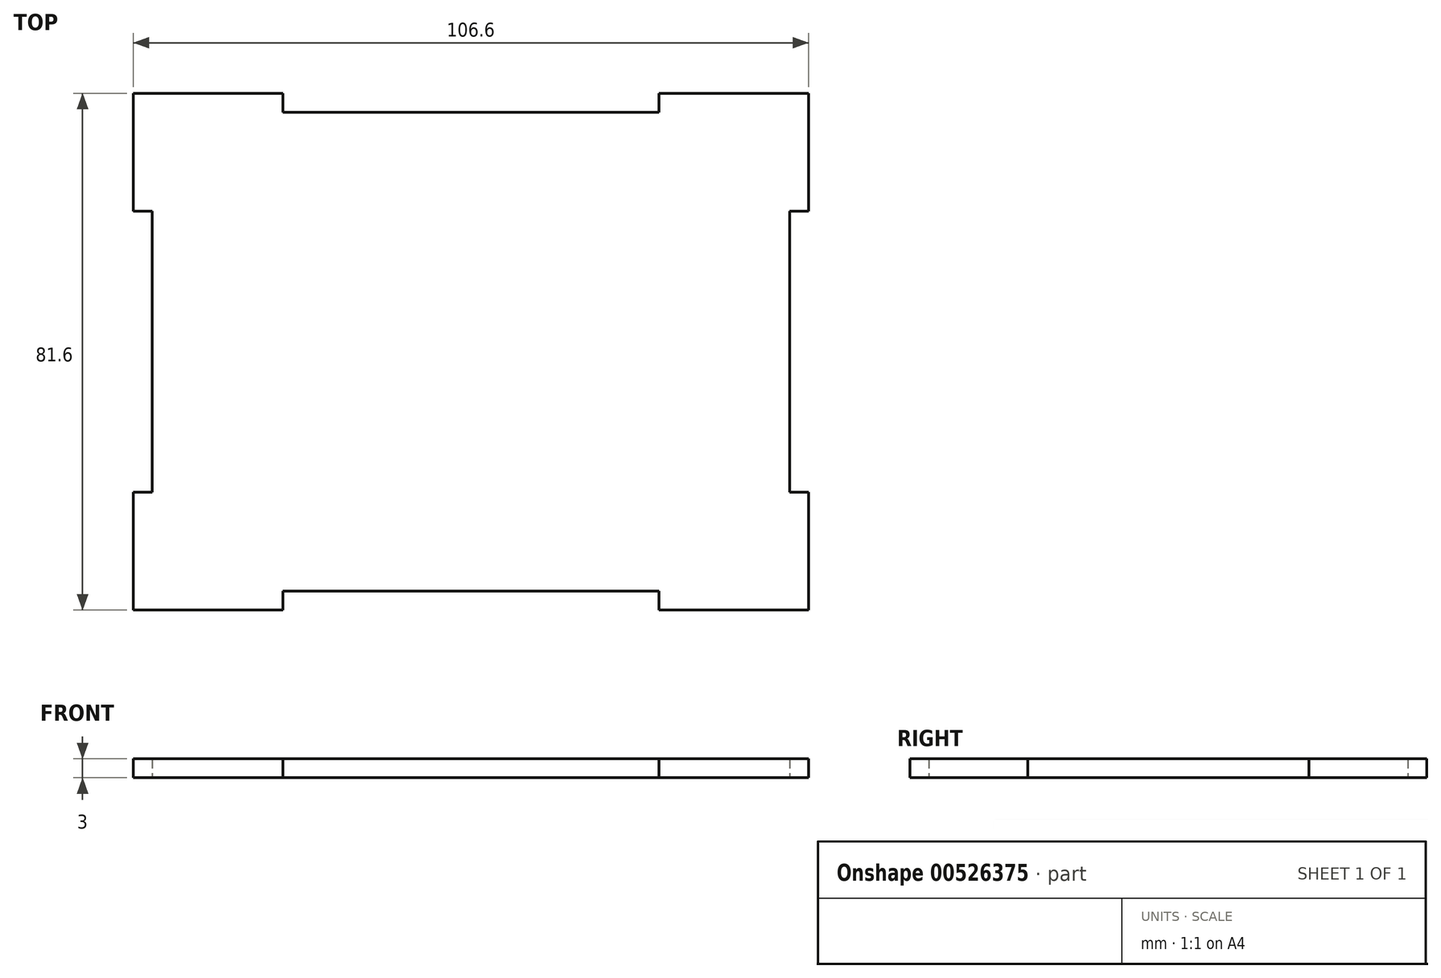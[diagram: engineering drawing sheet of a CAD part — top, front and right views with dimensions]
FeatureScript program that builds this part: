
annotation { "Feature Type Name" : "Feature", "Feature Type Description" : "" }
export const myFeature = defineFeature(function(context is Context, id is Id, definition is map)
    precondition{}
    {
        {
            assignVariable(context, id + "F0", {"name" : "thickness", "anyValue" : 3});
        }
        {
            var Q0;
            Q0=qCreatedBy(makeId("Top.planeOp"),FACE);
            var sketch = newSketch(context, id + "F1", { "sketchPlane" : qUnion([Q0])});
            skLineSegment(sketch, "E0", {"start": v(-53, 40.5) * mm, "end": v(-53, 22.5) * mm, "construction": true});
            skLineSegment(sketch, "E1", {"start": v(-53, 22.5) * mm, "end": v(-50, 22.5) * mm, "construction": true});
            skLineSegment(sketch, "E2", {"start": v(-30, 37.5) * mm, "end": v(-30, 40.5) * mm, "construction": true});
            skLineSegment(sketch, "E3", {"start": v(-30, 40.5) * mm, "end": v(-53, 40.5) * mm, "construction": true});
            skLineSegment(sketch, "E4", {"start": v(-50, 22.5) * mm, "end": v(-50, 0) * mm, "construction": true});
            skLineSegment(sketch, "E5", {"start": v(-30, 37.5) * mm, "end": v(0, 37.5) * mm, "construction": true});
            skLineSegment(sketch, "E6.MirrorCS", {"start": v(50, 22.5) * mm, "end": v(50, 0) * mm, "construction": true});
            skLineSegment(sketch, "E7.MirrorCS", {"start": v(30, 37.5) * mm, "end": v(0, 37.5) * mm, "construction": true});
            skLineSegment(sketch, "E8.MirrorCS", {"start": v(30, 37.5) * mm, "end": v(30, 40.5) * mm, "construction": true});
            skLineSegment(sketch, "E9.MirrorCS", {"start": v(53, 22.5) * mm, "end": v(50, 22.5) * mm, "construction": true});
            skLineSegment(sketch, "E10.MirrorCS", {"start": v(30, 40.5) * mm, "end": v(53, 40.5) * mm, "construction": true});
            skLineSegment(sketch, "E11.MirrorCS", {"start": v(53, 40.5) * mm, "end": v(53, 22.5) * mm, "construction": true});
            skLineSegment(sketch, "E12.MirrorCS", {"start": v(-30, -37.5) * mm, "end": v(0, -37.5) * mm, "construction": true});
            skLineSegment(sketch, "E13.MirrorCS", {"start": v(30, -40.5) * mm, "end": v(53, -40.5) * mm, "construction": true});
            skLineSegment(sketch, "E14.MirrorCS", {"start": v(-53, -40.5) * mm, "end": v(-53, -22.5) * mm, "construction": true});
            skLineSegment(sketch, "E15.MirrorCS", {"start": v(-30, -40.5) * mm, "end": v(-53, -40.5) * mm, "construction": true});
            skLineSegment(sketch, "E16.MirrorCS", {"start": v(-50, -22.5) * mm, "end": v(-50, 0) * mm, "construction": true});
            skLineSegment(sketch, "E17.MirrorCS", {"start": v(30, -37.5) * mm, "end": v(0, -37.5) * mm, "construction": true});
            skLineSegment(sketch, "E18.MirrorCS", {"start": v(53, -40.5) * mm, "end": v(53, -22.5) * mm, "construction": true});
            skLineSegment(sketch, "E19.MirrorCS", {"start": v(30, -37.5) * mm, "end": v(30, -40.5) * mm, "construction": true});
            skLineSegment(sketch, "E20.MirrorCS", {"start": v(53, -22.5) * mm, "end": v(50, -22.5) * mm, "construction": true});
            skLineSegment(sketch, "E21.MirrorCS", {"start": v(-30, -37.5) * mm, "end": v(-30, -40.5) * mm, "construction": true});
            skLineSegment(sketch, "E22.MirrorCS", {"start": v(50, -22.5) * mm, "end": v(50, 0) * mm, "construction": true});
            skLineSegment(sketch, "E23.MirrorCS", {"start": v(-53, -22.5) * mm, "end": v(-50, -22.5) * mm, "construction": true});
            skLineSegment(sketch, "E24.0", {"start": v(-29.7, 37.8) * mm, "end": v(-29.7, 40.8) * mm});
            skLineSegment(sketch, "E24.1", {"start": v(29.7, -37.8) * mm, "end": v(0, -37.8) * mm});
            skLineSegment(sketch, "E24.2", {"start": v(-29.7, -37.8) * mm, "end": v(0, -37.8) * mm});
            skLineSegment(sketch, "E24.3", {"start": v(-29.7, -37.8) * mm, "end": v(-29.7, -40.8) * mm});
            skLineSegment(sketch, "E24.4", {"start": v(-29.7, -40.8) * mm, "end": v(-53.3, -40.8) * mm});
            skLineSegment(sketch, "E24.5", {"start": v(-53.3, -40.8) * mm, "end": v(-53.3, -22.2) * mm});
            skLineSegment(sketch, "E24.6", {"start": v(-53.3, -22.2) * mm, "end": v(-50.3, -22.2) * mm});
            skLineSegment(sketch, "E24.7", {"start": v(-53.3, 40.8) * mm, "end": v(-53.3, 22.2) * mm});
            skLineSegment(sketch, "E24.8", {"start": v(-53.3, 22.2) * mm, "end": v(-50.3, 22.2) * mm});
            skLineSegment(sketch, "E24.9", {"start": v(-50.3, 22.2) * mm, "end": v(-50.3, 0) * mm});
            skLineSegment(sketch, "E24.10", {"start": v(-50.3, -22.2) * mm, "end": v(-50.3, 0) * mm});
            skLineSegment(sketch, "E24.11", {"start": v(29.7, -37.8) * mm, "end": v(29.7, -40.8) * mm});
            skLineSegment(sketch, "E24.12", {"start": v(-29.7, 40.8) * mm, "end": v(-53.3, 40.8) * mm});
            skLineSegment(sketch, "E24.13", {"start": v(29.7, -40.8) * mm, "end": v(53.3, -40.8) * mm});
            skLineSegment(sketch, "E24.14", {"start": v(53.3, -40.8) * mm, "end": v(53.3, -22.2) * mm});
            skLineSegment(sketch, "E24.15", {"start": v(53.3, -22.2) * mm, "end": v(50.3, -22.2) * mm});
            skLineSegment(sketch, "E24.16", {"start": v(50.3, -22.2) * mm, "end": v(50.3, 0) * mm});
            skLineSegment(sketch, "E24.17", {"start": v(50.3, 22.2) * mm, "end": v(50.3, 0) * mm});
            skLineSegment(sketch, "E24.18", {"start": v(53.3, 22.2) * mm, "end": v(50.3, 22.2) * mm});
            skLineSegment(sketch, "E24.19", {"start": v(53.3, 40.8) * mm, "end": v(53.3, 22.2) * mm});
            skLineSegment(sketch, "E24.20", {"start": v(29.7, 40.8) * mm, "end": v(53.3, 40.8) * mm});
            skLineSegment(sketch, "E24.21", {"start": v(29.7, 37.8) * mm, "end": v(29.7, 40.8) * mm});
            skLineSegment(sketch, "E24.22", {"start": v(29.7, 37.8) * mm, "end": v(0, 37.8) * mm});
            skLineSegment(sketch, "E24.23", {"start": v(-29.7, 37.8) * mm, "end": v(0, 37.8) * mm});
            skSolve(sketch);
        }
        {
            var Q0;
            Q0 = qSketchRegion(id + "F1", true);
            extrude(context, id + "F2", {"entities" : qUnion([Q0]), "depth" : (getVariable(context, 'thickness')) * mm, "offsetDistance" : 25 * mm});
        }
    });
